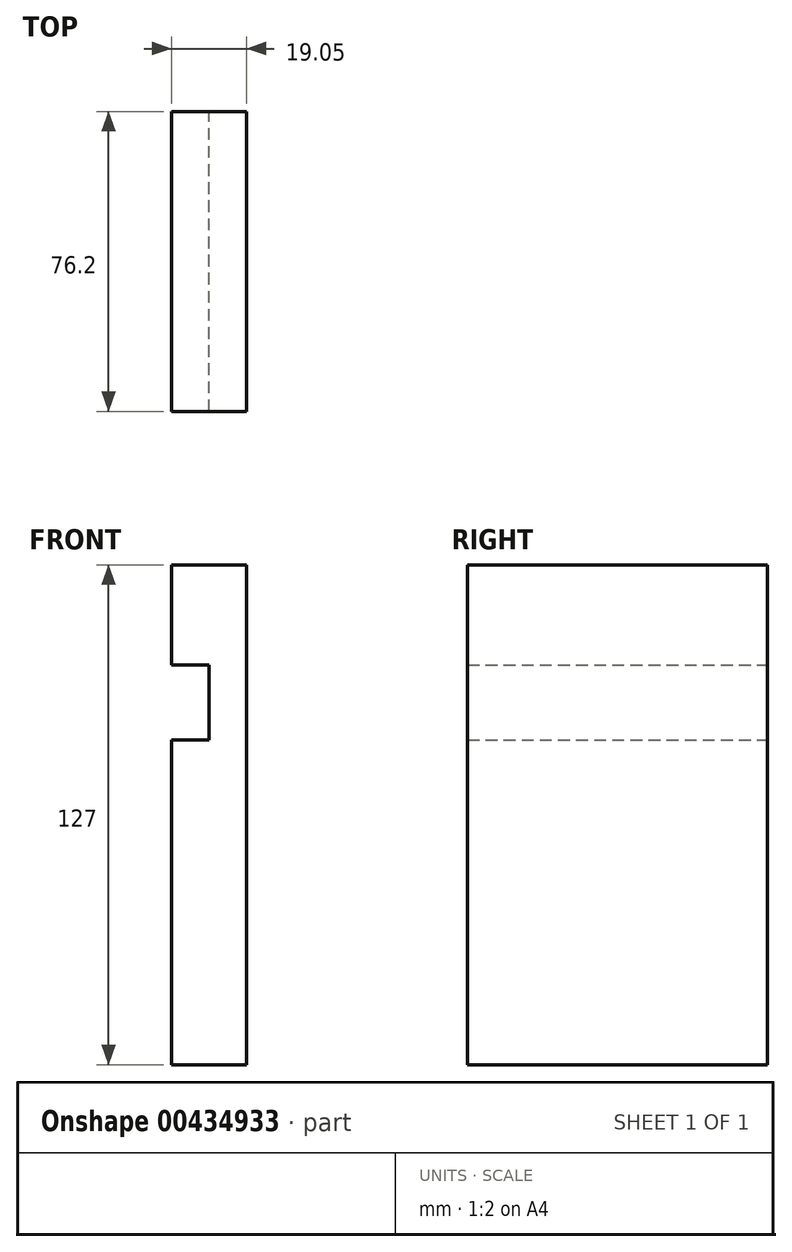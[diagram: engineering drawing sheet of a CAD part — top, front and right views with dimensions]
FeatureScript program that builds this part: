
annotation { "Feature Type Name" : "Feature", "Feature Type Description" : "" }
export const myFeature = defineFeature(function(context is Context, id is Id, definition is map)
    precondition{}
    {
        {
            var Q0;
            Q0=qCreatedBy(makeId("Front.planeOp"),FACE);
            var sketch = newSketch(context, id + "F0", { "sketchPlane" : qUnion([Q0])});
            skLineSegment(sketch, "E0", {"start": v(36.44, -72.13) * mm, "end": v(36.44, 54.87) * mm});
            skLineSegment(sketch, "E1", {"start": v(36.44, -72.13) * mm, "end": v(17.39, -72.13) * mm});
            skLineSegment(sketch, "E2", {"start": v(36.44, 54.87) * mm, "end": v(17.39, 54.87) * mm});
            skLineSegment(sketch, "E3", {"start": v(17.39, 54.87) * mm, "end": v(17.39, 29.47) * mm});
            skLineSegment(sketch, "E4", {"start": v(17.39, 29.47) * mm, "end": v(26.91, 29.47) * mm});
            skLineSegment(sketch, "E5", {"start": v(26.91, 29.47) * mm, "end": v(26.91, 10.42) * mm});
            skLineSegment(sketch, "E6", {"start": v(26.91, 10.42) * mm, "end": v(17.39, 10.42) * mm});
            skLineSegment(sketch, "E7", {"start": v(17.39, 10.42) * mm, "end": v(17.39, -72.13) * mm});
            skSolve(sketch);
        }
        {
            var Q0;
            Q0=makeQuery(id+"F0.imprint","IMPRINT",FACE,{"disambiguationData":[TD([[makeQuery(id+"F0.imprint","IMPRINT",EDGE,{"derivedFrom":sQuery(id+"F0.wireOp",EDGE,"E0")}),1.0]])]});
            extrude(context, id + "F1", {"entities" : qUnion([Q0]), "depth" : 76.2 * mm});
        }
    });
